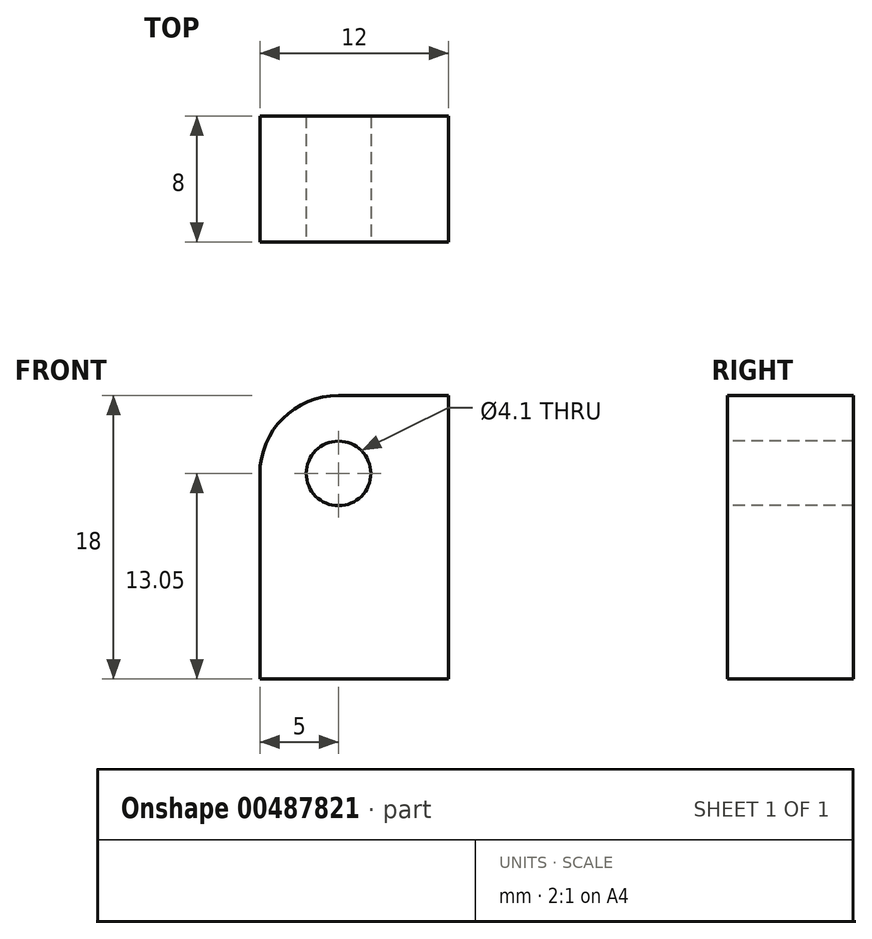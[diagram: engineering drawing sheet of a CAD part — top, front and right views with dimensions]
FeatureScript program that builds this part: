
annotation { "Feature Type Name" : "Feature", "Feature Type Description" : "" }
export const myFeature = defineFeature(function(context is Context, id is Id, definition is map)
    precondition{}
    {
        {
            var Q0;
            Q0=qCreatedBy(makeId("Front.planeOp"),FACE);
            var sketch = newSketch(context, id + "F0", { "sketchPlane" : qUnion([Q0])});
            skLineSegment(sketch, "E0.bottom", {"start": v(0, 0) * mm, "end": v(12, 0) * mm});
            skLineSegment(sketch, "E0.top", {"start": v(0, -18) * mm, "end": v(12, -18) * mm});
            skLineSegment(sketch, "E0.left", {"start": v(0, 0) * mm, "end": v(0, -18) * mm});
            skLineSegment(sketch, "E0.right", {"start": v(12, 0) * mm, "end": v(12, -18) * mm});
            skSolve(sketch);
        }
        {
            var Q0;
            Q0 = qSketchRegion(id + "F0", true);
            extrude(context, id + "F1", {"entities" : qUnion([Q0]), "depth" : 8 * mm, "offsetDistance" : 25 * mm});
        }
        {
            var Q0;
            Q0=makeQuery(id+"F1.opExtrude","CAP_FACE",FACE,{"disambiguationData":[OSD([sQuery(id+"F0.wireOp",EDGE,"E0.bottom"),sQuery(id+"F0.wireOp",EDGE,"E0.top"),sQuery(id+"F0.wireOp",EDGE,"E0.left"),sQuery(id+"F0.wireOp",EDGE,"E0.right")])],"isStart":false});
            var sketch = newSketch(context, id + "F2", { "sketchPlane" : qUnion([Q0])});
            skCircle(sketch, "E1", {"center": v(5, -4.95) * mm, "radius": 2.05 * mm});
            skSolve(sketch);
        }
        {
            var Q0;
            Q0=makeQuery(id+"F2.imprint","IMPRINT",FACE,{"disambiguationData":[TD([[makeQuery(id+"F2.imprint","IMPRINT",EDGE,{"derivedFrom":sQuery(id+"F2.wireOp",EDGE,"E1")}),1.0]])]});
            extrude(context, id + "F3", {"entities" : qUnion([Q0]), "operationType" : NewBodyOperationType.REMOVE, "endBound" : BoundingType.THROUGH_ALL, "oppositeDirection" : true, "depth" : 25 * mm, "offsetDistance" : 25 * mm});
        }
        {
            var Q0;
            Q0=makeQuery(id+"F1.opExtrude","SWEPT_EDGE",EDGE,{"disambiguationData":[OSD([sQuery(id+"F0.wireOp",EDGE,"E0.bottom"),sQuery(id+"F0.wireOp",EDGE,"E0.left")])]});
            fillet(context, id + "F4", {"entities" : qUnion([Q0]), "radius" : 5 * mm, "tangentPropagation" : true, "allowEdgeOverflow" : false});
        }
    });
